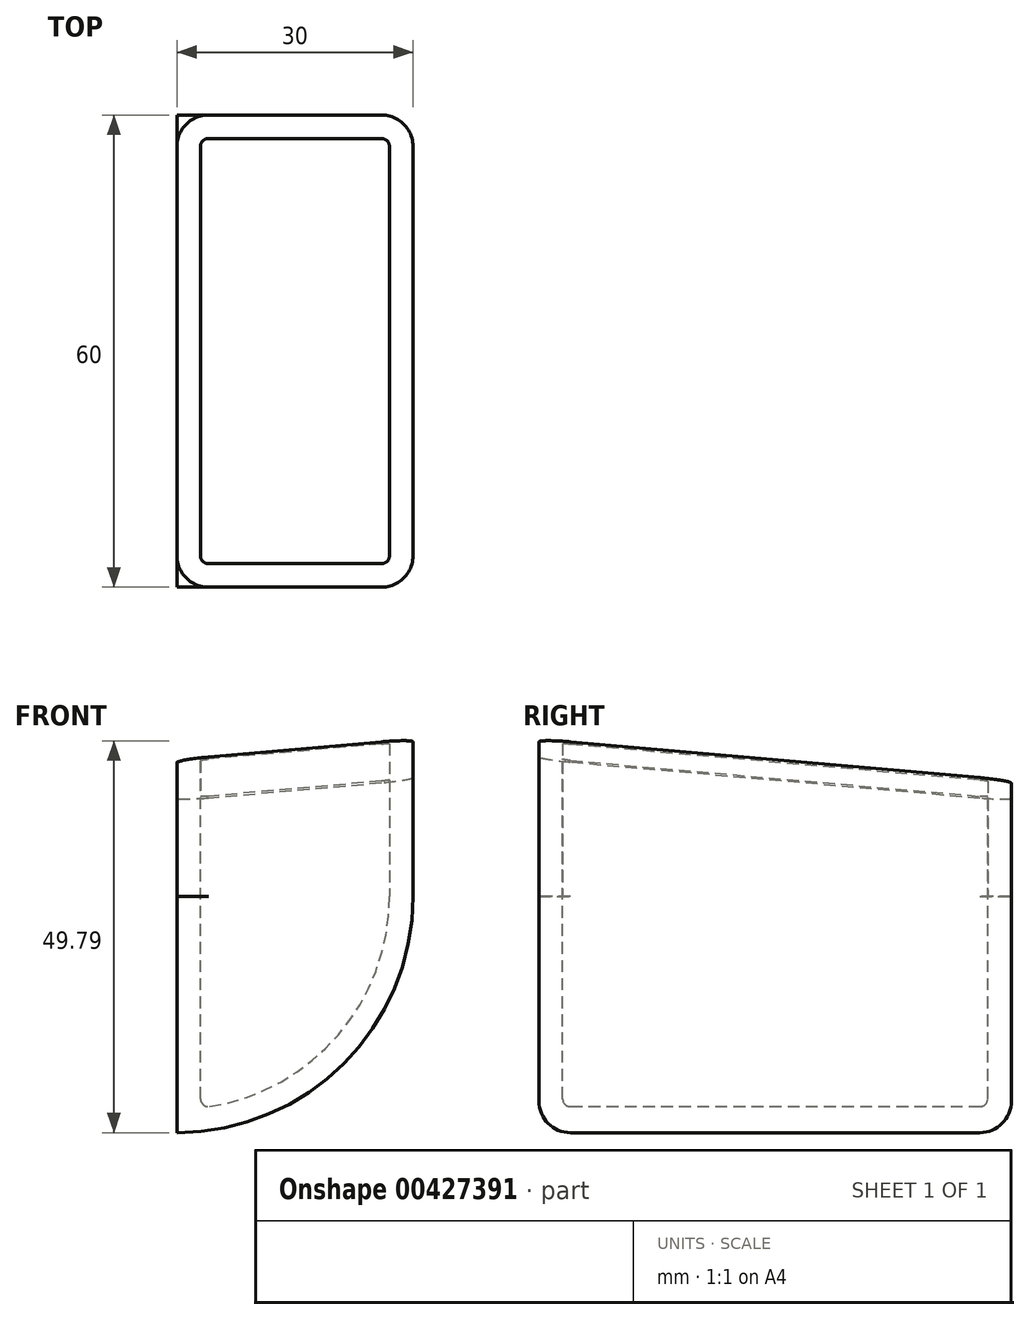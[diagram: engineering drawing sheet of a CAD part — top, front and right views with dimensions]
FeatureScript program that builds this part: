
annotation { "Feature Type Name" : "Feature", "Feature Type Description" : "" }
export const myFeature = defineFeature(function(context is Context, id is Id, definition is map)
    precondition{}
    {
        {
            var Q0;
            Q0=qCreatedBy(makeId("Front.planeOp"),FACE);
            var sketch = newSketch(context, id + "F0", { "sketchPlane" : qUnion([Q0])});
            skArc(sketch, "E0", {"start": v(0, -30) * mm, "mid": v(21.21, -21.21) * mm, "end": v(30, 0) * mm});
            skLineSegment(sketch, "E1", {"start": v(0, -30) * mm, "end": v(0, 0) * mm});
            skLineSegment(sketch, "E2", {"start": v(30, 0) * mm, "end": v(0, 0) * mm});
            skPoint(sketch, "E3.orphan", {"position": v(34.48, 0) * mm});
            skPoint(sketch, "E4.orphan", {"position": v(0, -36.55) * mm});
            skSolve(sketch);
        }
        {
            var Q0;
            Q0=makeQuery(id+"F0.imprint","IMPRINT",FACE,{"disambiguationData":[TD([[makeQuery(id+"F0.imprint","IMPRINT",EDGE,{"derivedFrom":sQuery(id+"F0.wireOp",EDGE,"E0")}),1.0]])]});
            extrude(context, id + "F1", {"entities" : qUnion([Q0]), "endBound" : BoundingType.SYMMETRIC, "depth" : 60 * mm});
        }
        {
            var Q0;
            Q0=makeQuery(id+"F1.opExtrude","SWEPT_FACE",FACE,{"disambiguationData":[OSD([sQuery(id+"F0.wireOp",EDGE,"E2")])]});
            shell(context, id + "F2", {"entities" : qUnion([Q0]), "thickness" : 3 * mm});
        }
        {
            var Q0;
            {var subQ0=sQuery(id+"F0.wireOp",EDGE,"E0");Q0=makeQuery(id+"F2.opShell","OFFSET_EDGE",EDGE,{"disambiguationData":[OSD([subQ0]),TDD([makeQuery(id+"F1.opExtrude","CAP_EDGE",EDGE,{"disambiguationData":[OSD([subQ0])],"isStart":false})])]});}
            var Q1;
            {var subQ0=sQuery(id+"F0.wireOp",EDGE,"E0");Q1=makeQuery(id+"F2.opShell","OFFSET_EDGE",EDGE,{"disambiguationData":[OSD([subQ0]),TDD([makeQuery(id+"F1.opExtrude","CAP_EDGE",EDGE,{"disambiguationData":[OSD([subQ0])],"isStart":true})])]});}
            fillet(context, id + "F3", {"entities" : qUnion([Q0, Q1]), "radius" : 1 * mm, "tangentPropagation" : true, "allowEdgeOverflow" : false});
        }
        {
            var Q0;
            Q0=makeQuery(id+"F1.opExtrude","CAP_EDGE",EDGE,{"disambiguationData":[OSD([sQuery(id+"F0.wireOp",EDGE,"E0")])],"isStart":false});
            var Q1;
            Q1=makeQuery(id+"F1.opExtrude","CAP_EDGE",EDGE,{"disambiguationData":[OSD([sQuery(id+"F0.wireOp",EDGE,"E0")])],"isStart":true});
            fillet(context, id + "F4", {"entities" : qUnion([Q0, Q1]), "radius" : 4 * mm, "tangentPropagation" : true, "allowEdgeOverflow" : false});
        }
        {
            var Q0;
            Q0=makeQuery(id+"F1.opExtrude","SWEPT_FACE",FACE,{"disambiguationData":[OSD([sQuery(id+"F0.wireOp",EDGE,"E2")])]});
            var sketch = newSketch(context, id + "F5", { "sketchPlane" : qUnion([Q0])});
            skLineSegment(sketch, "E5.0", {"start": v(26, -30) * mm, "end": v(0, -30) * mm});
            skPoint(sketch, "E6.0", {"position": v(28.83, -28.83) * mm});
            skArc(sketch, "E7.0", {"start": v(27, -26) * mm, "mid": v(26.7, -26.7) * mm, "end": v(26, -27) * mm});
            skLineSegment(sketch, "E8.0", {"start": v(26, -27) * mm, "end": v(3, -27) * mm});
            skArc(sketch, "E9.0", {"start": v(26, -30) * mm, "mid": v(28.83, -28.83) * mm, "end": v(30, -26) * mm});
            skLineSegment(sketch, "E10.0", {"start": v(30, -26) * mm, "end": v(30, 26) * mm});
            skLineSegment(sketch, "E11.0", {"start": v(27, -26) * mm, "end": v(27, 26) * mm});
            skLineSegment(sketch, "E12.0", {"start": v(3, -27) * mm, "end": v(3, 27) * mm});
            skLineSegment(sketch, "E13.0", {"start": v(0, -30) * mm, "end": v(0, 30) * mm});
            skLineSegment(sketch, "E14.0", {"start": v(26, 30) * mm, "end": v(0, 30) * mm});
            skLineSegment(sketch, "E15.0", {"start": v(26, 27) * mm, "end": v(3, 27) * mm});
            skArc(sketch, "E16.0", {"start": v(26, 27) * mm, "mid": v(26.7, 26.7) * mm, "end": v(27, 26) * mm});
            skArc(sketch, "E17.0", {"start": v(30, 26) * mm, "mid": v(28.83, 28.83) * mm, "end": v(26, 30) * mm});
            skSolve(sketch);
        }
        {
            var Q0;
            Q0=makeQuery(id+"F5.imprint","IMPRINT",FACE,{"disambiguationData":[TD([[makeQuery(id+"F5.imprint","IMPRINT",EDGE,{"derivedFrom":sQuery(id+"F5.wireOp",EDGE,"E5.0")}),-1.0]])]});
            extrude(context, id + "F6", {"entities" : qUnion([Q0]), "operationType" : NewBodyOperationType.ADD, "depth" : 20 * mm});
        }
        {
            var Q0;
            Q0=makeQuery(id+"F6.boolean.opBoolean","MERGE",FACE,{"derivedFrom":[makeQuery(id+"F1.opExtrude","SWEPT_FACE",FACE,{"disambiguationData":[OSD([sQuery(id+"F0.wireOp",EDGE,"E1")])]}),makeQuery(id+"F6.opExtrude","SWEPT_FACE",FACE,{"disambiguationData":[OSD([sQuery(id+"F5.wireOp",EDGE,"E13.0")])]})]});
            var sketch = newSketch(context, id + "F7", { "sketchPlane" : qUnion([Q0])});
            skLineSegment(sketch, "E18.0", {"start": v(30, 20) * mm, "end": v(-30, 20) * mm});
            skLineSegment(sketch, "E19", {"start": v(-30, 20) * mm, "end": v(-30, 14.75) * mm});
            skLineSegment(sketch, "E20", {"start": v(-30, 14.75) * mm, "end": v(30, 20) * mm});
            skSolve(sketch);
        }
        {
            var Q0;
            Q0=makeQuery(id+"F7.imprint","IMPRINT",FACE,{"disambiguationData":[TD([[makeQuery(id+"F7.imprint","IMPRINT",EDGE,{"derivedFrom":sQuery(id+"F7.wireOp",EDGE,"E18.0")}),1.0]])]});
            extrude(context, id + "F8", {"entities" : qUnion([Q0]), "operationType" : NewBodyOperationType.REMOVE, "oppositeDirection" : true, "depth" : 40 * mm});
        }
        {
            var Q0;
            {var subQ0=sQuery(id+"F0.wireOp",EDGE,"E1");Q0=makeQuery(id+"F6.boolean.opBoolean","MERGE",EDGE,{"derivedFrom":[makeQuery(id+"F2.opShell","OFFSET_EDGE",EDGE,{"disambiguationData":[OSD([subQ0]),TDD([makeQuery(id+"F1.opExtrude","CAP_EDGE",EDGE,{"disambiguationData":[OSD([subQ0])],"isStart":false})])]}),makeQuery(id+"F6.opExtrude","SWEPT_EDGE",EDGE,{"disambiguationData":[OSD([sQuery(id+"F5.wireOp",EDGE,"E8.0"),sQuery(id+"F5.wireOp",EDGE,"E12.0")])]})]});}
            fillet(context, id + "F9", {"entities" : qUnion([Q0]), "radius" : 1 * mm, "tangentPropagation" : true, "allowEdgeOverflow" : false});
        }
        {
            var Q0;
            Q0=qCreatedBy(makeId("Top.planeOp"),FACE);
            cPlane(context, id + "F10", {"entities" : qUnion([Q0]), "cplaneType" : CPlaneType.OFFSET, "offset" : 25 * mm, "width" : 150 * mm, "height" : 150 * mm});
        }
        {
            var Q0;
            Q0=qCreatedBy(id+"F10.planeOp",FACE);
            var sketch = newSketch(context, id + "F11", { "sketchPlane" : qUnion([Q0])});
            skPoint(sketch, "E21.visualSharp", {"position": v(0, 30) * mm});
            skArc(sketch, "E21.filletArc", {"start": v(4, 30) * mm, "mid": v(1.17, 28.83) * mm, "end": v(0, 26) * mm});
            skPoint(sketch, "E22.visualSharp", {"position": v(0, -30) * mm});
            skArc(sketch, "E22.filletArc", {"start": v(0, -26) * mm, "mid": v(1.17, -28.83) * mm, "end": v(4, -30) * mm});
            skLineSegment(sketch, "E23", {"start": v(0, 26) * mm, "end": v(0, 30) * mm});
            skLineSegment(sketch, "E24", {"start": v(0, 30) * mm, "end": v(4, 30) * mm});
            skLineSegment(sketch, "E25", {"start": v(0, -30) * mm, "end": v(0, -26) * mm});
            skLineSegment(sketch, "E26", {"start": v(0, -30) * mm, "end": v(4, -30) * mm});
            skPoint(sketch, "E27.0.start.orphan", {"position": v(26, 30) * mm});
            skPoint(sketch, "E28.0.start.orphan", {"position": v(26, -30) * mm});
            skSolve(sketch);
        }
        {
            var Q0;
            Q0 = qSketchRegion(id + "F11", true);
            extrude(context, id + "F12", {"entities" : qUnion([Q0]), "operationType" : NewBodyOperationType.REMOVE, "oppositeDirection" : true, "depth" : 25 * mm});
        }
        {
            var Q0;
            {var subQ0=sQuery(id+"F5.wireOp",EDGE,"E5.0");Q0=makeQuery(id+"F8.boolean.opBoolean","MERGE",EDGE,{"derivedFrom":[makeQuery(id+"F6.opExtrude","CAP_EDGE",EDGE,{"disambiguationData":[OSD([subQ0])],"isStart":false}),makeQuery(id+"F8.opExtrude","SWEPT_EDGE",EDGE,{"disambiguationData":[OSD([sQuery(id+"F0.wireOp",EDGE,"E1"),subQ0,sQuery(id+"F5.wireOp",EDGE,"E13.0"),sQuery(id+"F7.wireOp",EDGE,"E18.0"),sQuery(id+"F7.wireOp",EDGE,"E20")])]})]});}
            cPlane(context, id + "F13", {"entities" : qUnion([Q0]), "cplaneType" : CPlaneType.LINE_ANGLE, "offset" : 25 * mm, "angle" : 5 * degree, "width" : 150 * mm, "height" : 150 * mm});
        }
        {
            var Q0;
            Q0=qCreatedBy(id+"F13.planeOp",FACE);
            var sketch = newSketch(context, id + "F14", { "sketchPlane" : qUnion([Q0])});
            skLineSegment(sketch, "E29.0", {"start": v(4, 17.3) * mm, "end": v(0, 17.3) * mm});
            skLineSegment(sketch, "E30.0", {"start": v(26, 17.3) * mm, "end": v(4, 17.3) * mm});
            skLineSegment(sketch, "E31.0", {"start": v(30, 17.3) * mm, "end": v(26, 17.3) * mm});
            skLineSegment(sketch, "E32", {"start": v(30, 17.3) * mm, "end": v(0, 14.68) * mm});
            skLineSegment(sketch, "E33.0", {"start": v(0, 14.68) * mm, "end": v(0, 17.3) * mm});
            skPoint(sketch, "E34.orphan", {"position": v(0, -2.27) * mm});
            skSolve(sketch);
        }
        {
            var Q0;
            Q0=makeQuery(id+"F14.imprint","IMPRINT",FACE,{"disambiguationData":[TD([[makeQuery(id+"F14.imprint","IMPRINT",EDGE,{"derivedFrom":sQuery(id+"F14.wireOp",EDGE,"E29.0")}),1.0]])]});
            extrude(context, id + "F15", {"entities" : qUnion([Q0]), "operationType" : NewBodyOperationType.REMOVE, "oppositeDirection" : true, "depth" : 70 * mm});
        }
    });
